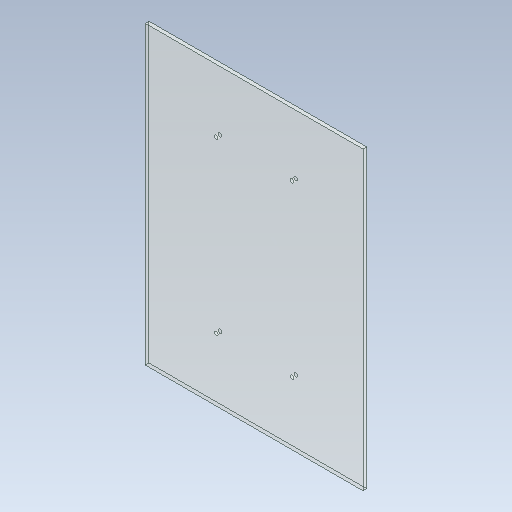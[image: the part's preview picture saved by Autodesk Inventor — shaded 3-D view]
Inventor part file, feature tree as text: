
AUTODESK INVENTOR PART (.ipt)
format: ipt  version: 2021 (Build 250183000, 183)  size: 104,448 bytes
history: native  units: mm
features: other x9, sketch x2, extrude x1, hole x1
ambient origin geometry x8: Origin, YZ Plane, XZ Plane, XY Plane, X Axis, Y Axis, Z Axis, Center Point
bodies: Body1 (feature_tree)
feature tree (13):
  other  "Sólido1"
  extrude  "Extrusão1"  Depth=242.0mm
  hole  "Furo1"  [1 undecoded]
  sketch  "Esboço1"  dims[d0=178.0mm d1=242.0mm]
  sketch  "Esboço2"  dims[d2=3.0mm d3=0.0mm d4=3.0mm d5=42.0mm d6=4.0mm d7=2.0mm d8=90.0deg d9=8.0mm d10=0.0mm]
  other  "Referência1"
  other  "Referência2"
  other  "Referência3"
  other  "Referência4"
  parser-record x1  (decoder bookkeeping rows leaked as tree rows — omitted from the tree; the rows remain in map.json)
  other  "Omni Robot.iam"
  other  "chapa lentral:1"
  other  "chapa lentral:2"
note: 1 required parameter value undecoded (feature->parameter linkage not recoverable at this tier; creation-order binding heuristic only, values carry confidence <= 0.55)
note: 1 file-system path scrubbed to <path> (originals preserved in map.json)
